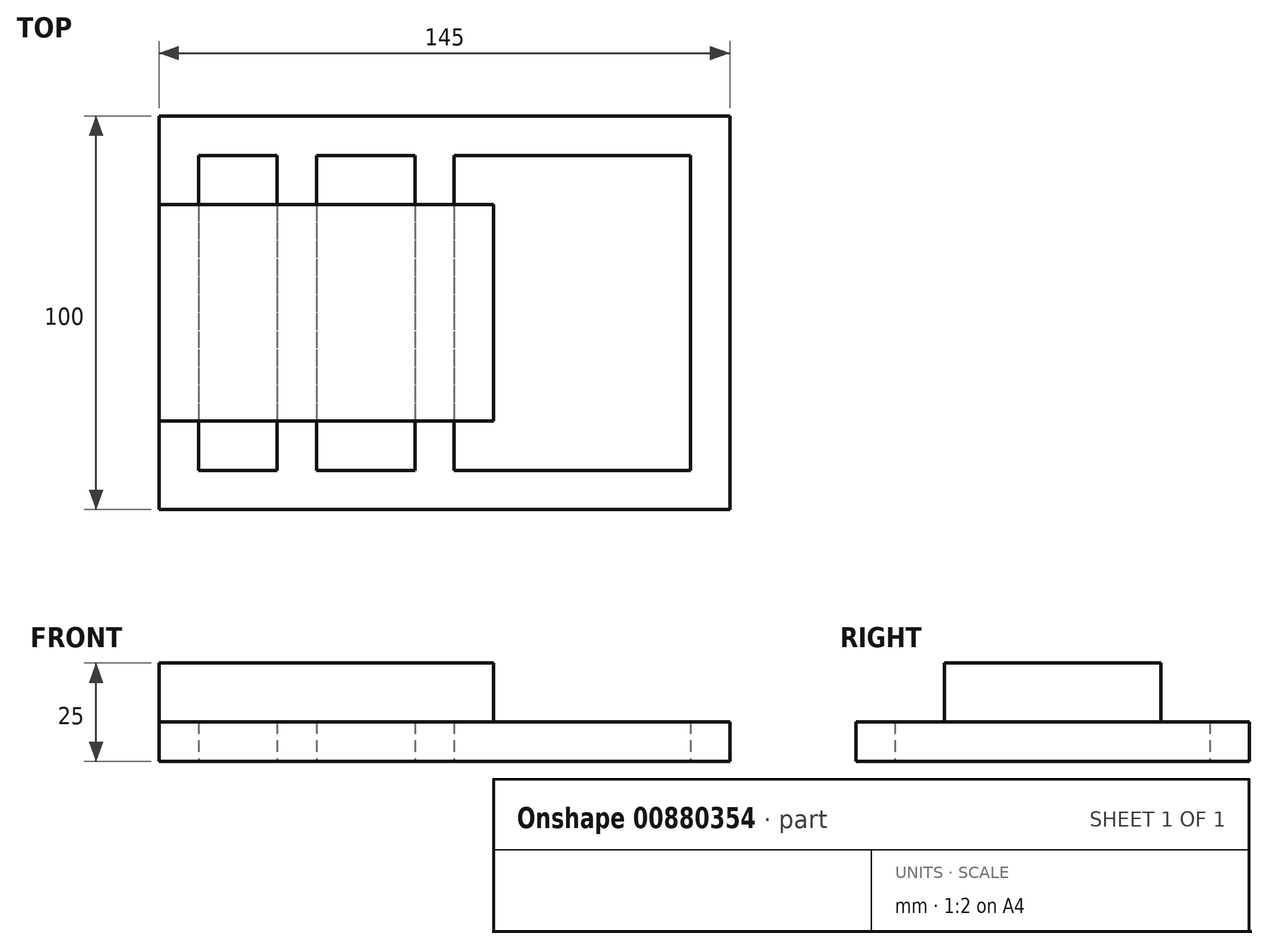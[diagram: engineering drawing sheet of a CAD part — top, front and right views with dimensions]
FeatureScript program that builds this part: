
annotation { "Feature Type Name" : "Feature", "Feature Type Description" : "" }
export const myFeature = defineFeature(function(context is Context, id is Id, definition is map)
    precondition{}
    {
        {
            var Q0;
            Q0=qCreatedBy(makeId("Top.planeOp"),FACE);
            var sketch = newSketch(context, id + "F0", { "sketchPlane" : qUnion([Q0])});
            skLineSegment(sketch, "E0.bottom", {"start": v(-72.5, 50) * mm, "end": v(72.5, 50) * mm});
            skLineSegment(sketch, "E0.top", {"start": v(-72.5, -50) * mm, "end": v(72.5, -50) * mm});
            skLineSegment(sketch, "E0.left", {"start": v(-72.5, 50) * mm, "end": v(-72.5, -50) * mm});
            skLineSegment(sketch, "E0.right", {"start": v(72.5, 50) * mm, "end": v(72.5, -50) * mm});
            skLineSegment(sketch, "E1.bottom", {"start": v(-62.5, 40) * mm, "end": v(62.5, 40) * mm});
            skLineSegment(sketch, "E1.top", {"start": v(-62.5, -40) * mm, "end": v(62.5, -40) * mm});
            skLineSegment(sketch, "E1.left", {"start": v(-62.5, 40) * mm, "end": v(-62.5, -40) * mm});
            skLineSegment(sketch, "E1.right", {"start": v(62.5, 40) * mm, "end": v(62.5, -40) * mm});
            skLineSegment(sketch, "E2.bottom", {"start": v(-42.5, 40) * mm, "end": v(-32.5, 40) * mm});
            skLineSegment(sketch, "E2.top", {"start": v(-42.5, -40) * mm, "end": v(-32.5, -40) * mm});
            skLineSegment(sketch, "E2.left", {"start": v(-42.5, 40) * mm, "end": v(-42.5, -40) * mm});
            skLineSegment(sketch, "E2.right", {"start": v(-32.5, 40) * mm, "end": v(-32.5, -40) * mm});
            skLineSegment(sketch, "E3.bottom", {"start": v(2.5, 40) * mm, "end": v(-7.5, 40) * mm});
            skLineSegment(sketch, "E3.top", {"start": v(2.5, -40) * mm, "end": v(-7.5, -40) * mm});
            skLineSegment(sketch, "E3.left", {"start": v(2.5, 40) * mm, "end": v(2.5, -40) * mm});
            skLineSegment(sketch, "E3.right", {"start": v(-7.5, 40) * mm, "end": v(-7.5, -40) * mm});
            skSolve(sketch);
        }
        {
            var Q0;
            Q0=makeQuery(id+"F0.imprint","IMPRINT",FACE,{"disambiguationData":[TD([[makeQuery(id+"F0.imprint","IMPRINT",EDGE,{"derivedFrom":sQuery(id+"F0.wireOp",EDGE,"E0.bottom")}),-1.0]])]});
            var Q1;
            {var subQ0=sQuery(id+"F0.wireOp",EDGE,"E2.left");Q1=makeQuery(id+"F0.imprint","IMPRINT",FACE,{"disambiguationData":[TD([[makeQuery(id+"F0.imprint","IMPRINT",EDGE,{"derivedFrom":subQ0}),1.0]])]});}
            var Q2;
            {var subQ0=sQuery(id+"F0.wireOp",EDGE,"E3.left");Q2=makeQuery(id+"F0.imprint","IMPRINT",FACE,{"disambiguationData":[TD([[makeQuery(id+"F0.imprint","IMPRINT",EDGE,{"derivedFrom":subQ0}),-1.0]])]});}
            extrude(context, id + "F1", {"entities" : qUnion([Q0, Q1, Q2]), "depth" : 10 * mm, "offsetDistance" : 25 * mm});
        }
        {
            var Q0;
            Q0=makeQuery(id+"F1.opExtrude","CAP_FACE",FACE,{"disambiguationData":[OSD([sQuery(id+"F0.wireOp",EDGE,"E0.bottom"),sQuery(id+"F0.wireOp",EDGE,"E0.top"),sQuery(id+"F0.wireOp",EDGE,"E0.left"),sQuery(id+"F0.wireOp",EDGE,"E0.right"),sQuery(id+"F0.wireOp",EDGE,"E1.bottom"),sQuery(id+"F0.wireOp",EDGE,"E1.top"),sQuery(id+"F0.wireOp",EDGE,"E1.left"),sQuery(id+"F0.wireOp",EDGE,"E1.right"),sQuery(id+"F0.wireOp",EDGE,"E2.left"),sQuery(id+"F0.wireOp",EDGE,"E2.right"),sQuery(id+"F0.wireOp",EDGE,"E3.left"),sQuery(id+"F0.wireOp",EDGE,"E3.right")])],"isStart":false});
            var sketch = newSketch(context, id + "F2", { "sketchPlane" : qUnion([Q0])});
            skLineSegment(sketch, "E4.bottom", {"start": v(-72.5, 27.5) * mm, "end": v(12.5, 27.5) * mm});
            skLineSegment(sketch, "E4.top", {"start": v(-72.5, -27.5) * mm, "end": v(12.5, -27.5) * mm});
            skLineSegment(sketch, "E4.left", {"start": v(-72.5, 27.5) * mm, "end": v(-72.5, -27.5) * mm});
            skLineSegment(sketch, "E4.right", {"start": v(12.5, 27.5) * mm, "end": v(12.5, -27.5) * mm});
            skSolve(sketch);
        }
        {
            var Q0;
            Q0 = qSketchRegion(id + "F2", true);
            extrude(context, id + "F3", {"entities" : qUnion([Q0]), "operationType" : NewBodyOperationType.ADD, "depth" : 15 * mm, "offsetDistance" : 25 * mm});
        }
    });
